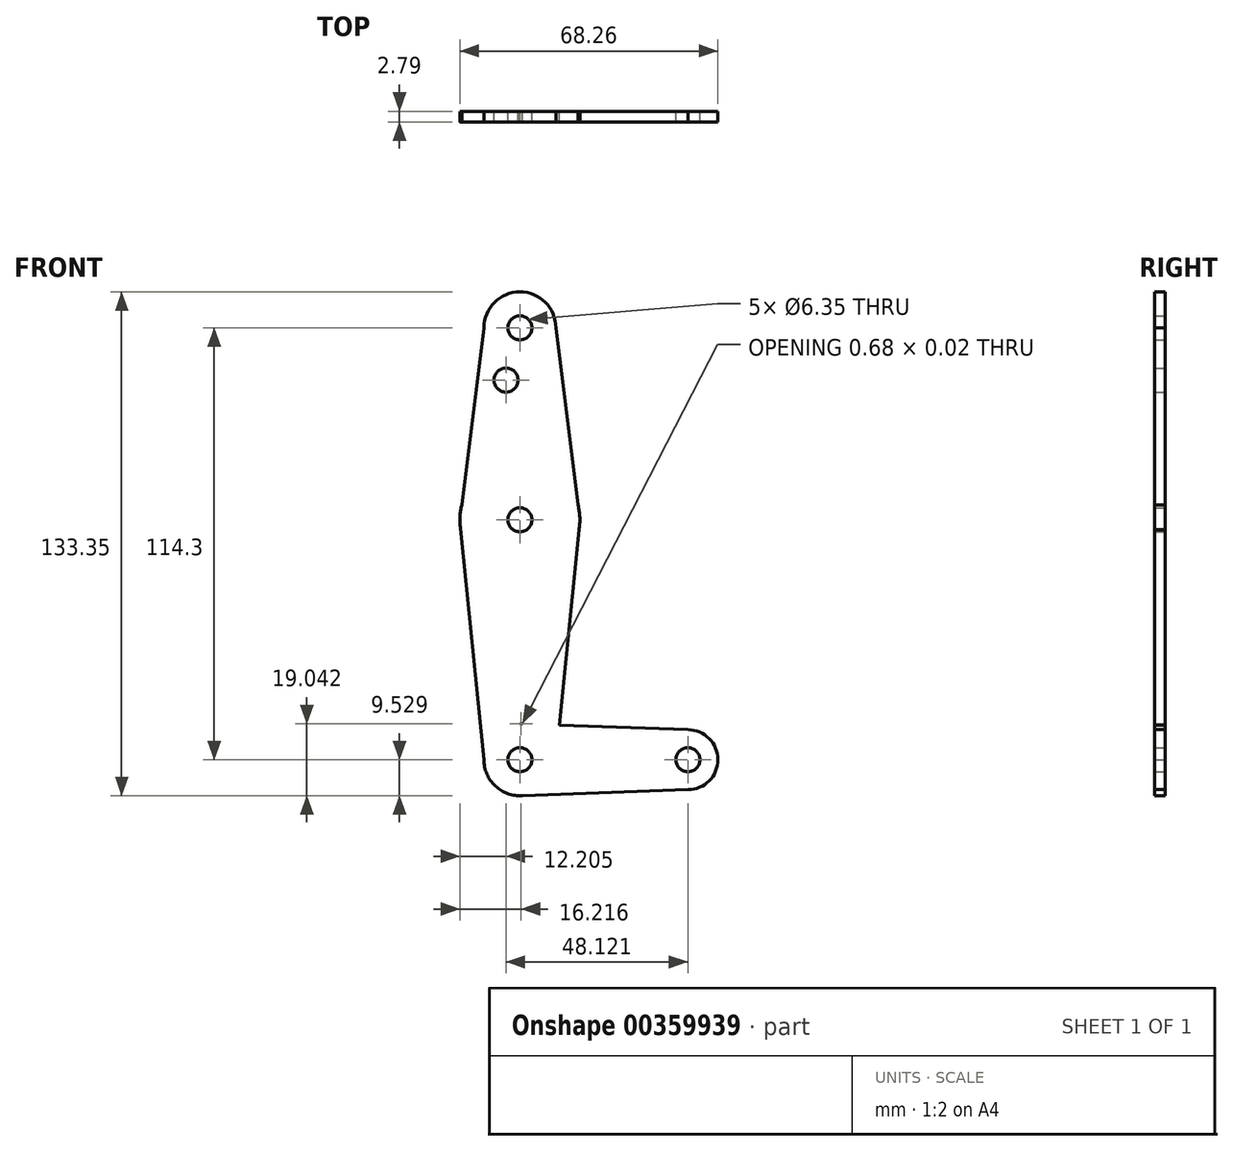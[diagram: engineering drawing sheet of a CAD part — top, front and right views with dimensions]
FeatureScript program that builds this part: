
annotation { "Feature Type Name" : "Feature", "Feature Type Description" : "" }
export const myFeature = defineFeature(function(context is Context, id is Id, definition is map)
    precondition{}
    {
        {
            var Q0;
            Q0=qCreatedBy(makeId("Front.planeOp"),FACE);
            var sketch = newSketch(context, id + "F0", { "sketchPlane" : qUnion([Q0])});
            skCircle(sketch, "E0", {"center": v(-22.2, 1.28) * mm, "radius": 15.88 * mm});
            skLineSegment(sketch, "E1", {"start": v(-22.2, 1.28) * mm, "end": v(-22.2, -62.22) * mm});
            skCircle(sketch, "E2", {"center": v(-22.2, 52.08) * mm, "radius": 9.53 * mm});
            skCircle(sketch, "E3", {"center": v(-22.2, -62.22) * mm, "radius": 9.53 * mm});
            skLineSegment(sketch, "E4", {"start": v(-22.2, -62.22) * mm, "end": v(22.25, -62.22) * mm});
            skCircle(sketch, "E5", {"center": v(22.25, -62.22) * mm, "radius": 7.94 * mm});
            skLineSegment(sketch, "E6", {"start": v(-22.2, 52.08) * mm, "end": v(-22.2, 1.28) * mm});
            skLineSegment(sketch, "E7", {"start": v(-12.68, 52.08) * mm, "end": v(-6.33, 1.28) * mm});
            skLineSegment(sketch, "E8", {"start": v(-31.73, 52.08) * mm, "end": v(-38.08, 1.28) * mm});
            skLineSegment(sketch, "E9", {"start": v(-37.92, -1) * mm, "end": v(-31.73, -62.22) * mm});
            skLineSegment(sketch, "E10", {"start": v(-6.56, -1.45) * mm, "end": v(-12.68, -62.22) * mm});
            skLineSegment(sketch, "E11", {"start": v(-22.2, -52.7) * mm, "end": v(22.25, -54.28) * mm});
            skLineSegment(sketch, "E12", {"start": v(-22.2, -71.75) * mm, "end": v(22.25, -70.16) * mm});
            skCircle(sketch, "E13", {"center": v(-22.2, 52.08) * mm, "radius": 3.18 * mm});
            skCircle(sketch, "E14", {"center": v(-25.87, 38.26) * mm, "radius": 3.18 * mm});
            skCircle(sketch, "E15", {"center": v(-22.2, 1.28) * mm, "radius": 3.18 * mm});
            skCircle(sketch, "E16", {"center": v(-22.2, -62.22) * mm, "radius": 3.18 * mm});
            skCircle(sketch, "E17", {"center": v(22.25, -62.22) * mm, "radius": 3.18 * mm});
            skLineSegment(sketch, "E18", {"start": v(-22.2, 1.74) * mm, "end": v(-22.2, 38.26) * mm});
            skSolve(sketch);
        }
        {
            var Q0;
            Q0 = qSketchRegion(id + "F0", true);
            var Q1;
            {var subQ3=sQuery(id+"F0.wireOp",EDGE,"E16");var subQ5=sQuery(id+"F0.wireOp",EDGE,"E1");var subQ6=makeQuery(id+"F0.imprint","INTERSECT",VERTEX,{"derivedFrom":[subQ5,subQ3]});Q1=makeQuery(id+"F0.imprint","IMPRINT",FACE,{"disambiguationData":[TD([[makeQuery(id+"F0.imprint","IMPRINT",EDGE,{"disambiguationData":[TD([[subQ6,1.0]])],"derivedFrom":subQ3}),-1.0]])]});}
            extrude(context, id + "F1", {"entities" : qUnion([Q0, Q1]), "depth" : 2.8 * mm});
        }
    });
